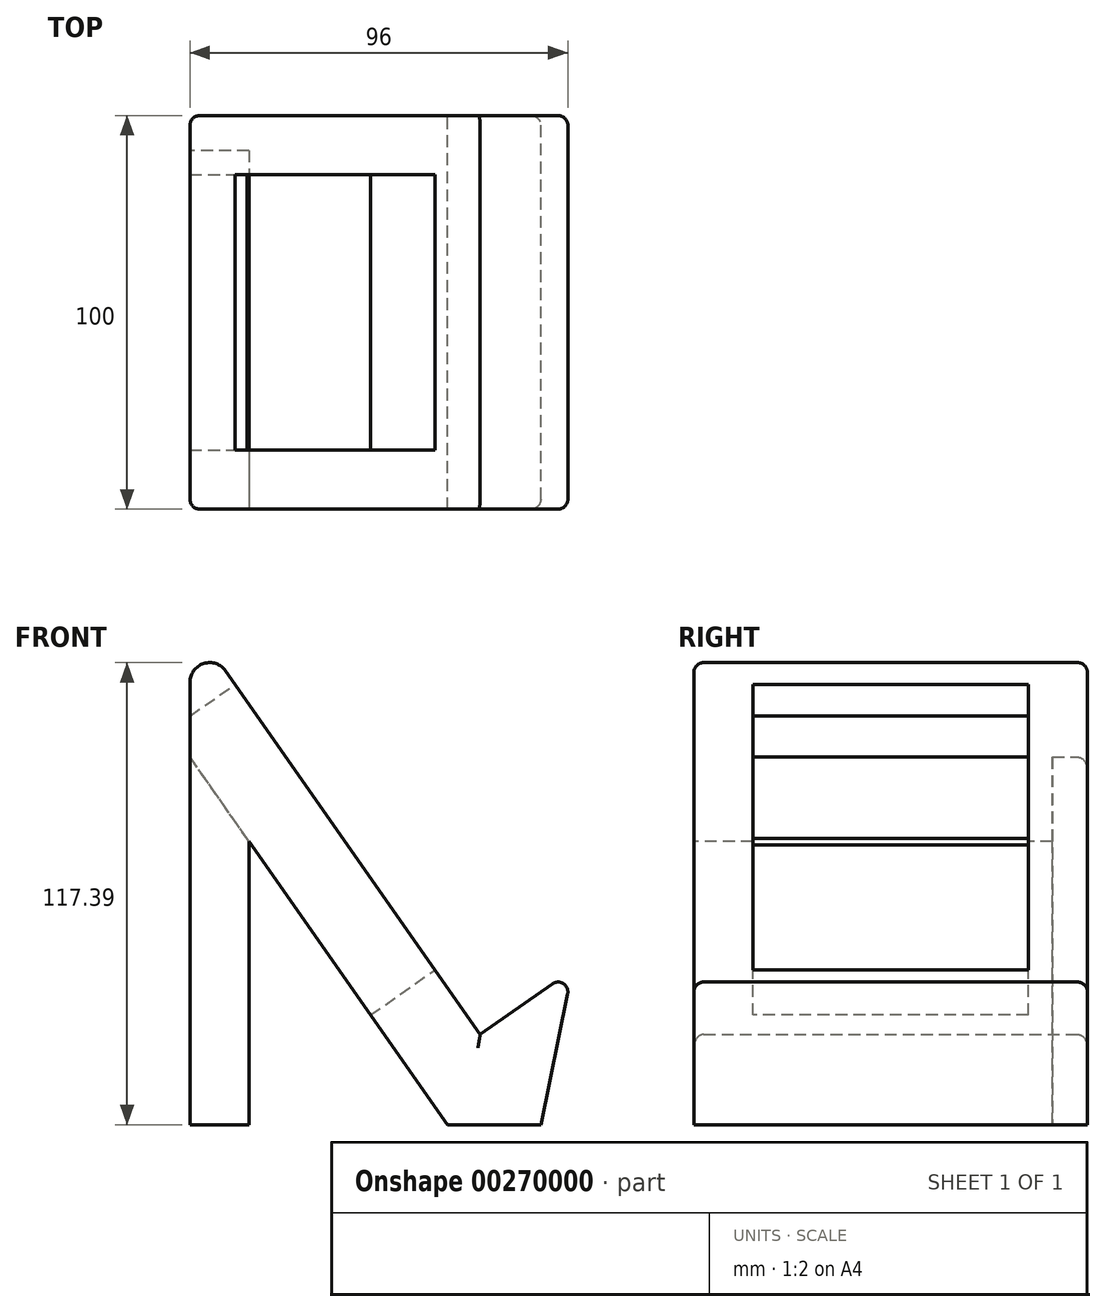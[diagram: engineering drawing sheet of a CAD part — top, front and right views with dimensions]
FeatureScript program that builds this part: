
annotation { "Feature Type Name" : "Feature", "Feature Type Description" : "" }
export const myFeature = defineFeature(function(context is Context, id is Id, definition is map)
    precondition{}
    {
        {
            var Q0;
            Q0=qCreatedBy(makeId("Front.planeOp"),FACE);
            var sketch = newSketch(context, id + "F0", { "sketchPlane" : qUnion([Q0])});
            skLineSegment(sketch, "E0", {"start": v(0, 0) * mm, "end": v(-73.74, 105.31) * mm});
            skLineSegment(sketch, "E1", {"start": v(15.38, -22.94) * mm, "end": v(-8.35, -22.94) * mm});
            skLineSegment(sketch, "E2", {"start": v(-8.35, -22.94) * mm, "end": v(-73.74, 70.44) * mm});
            skLineSegment(sketch, "E3", {"start": v(0, 0) * mm, "end": v(23.48, 16.44) * mm});
            skLineSegment(sketch, "E4", {"start": v(23.48, 16.44) * mm, "end": v(15.38, -22.94) * mm});
            skLineSegment(sketch, "E5", {"start": v(-73.74, 43.45) * mm, "end": v(-73.74, 105.31) * mm});
            skLineSegment(sketch, "E6", {"start": v(-73.74, -22.94) * mm, "end": v(-73.74, 43.45) * mm});
            skLineSegment(sketch, "E7", {"start": v(-73.74, -22.94) * mm, "end": v(-58.74, -22.94) * mm});
            skLineSegment(sketch, "E8", {"start": v(-58.74, -22.94) * mm, "end": v(-58.74, 83.9) * mm});
            skLineSegment(sketch, "E9", {"start": v(-58.74, -22.94) * mm, "end": v(-8.35, -22.94) * mm});
            skSolve(sketch);
        }
        {
            var Q0;
            {var subQ6=sQuery(id+"F0.wireOp",EDGE,"E1");Q0=makeQuery(id+"F0.imprint","IMPRINT",FACE,{"disambiguationData":[TD([[makeQuery(id+"F0.imprint","IMPRINT",EDGE,{"derivedFrom":subQ6}),-1.0]])]});}
            var Q1;
            {var subQ0=sQuery(id+"F0.wireOp",EDGE,"E5");var subQ1=sQuery(id+"F0.wireOp",EDGE,"E0");var subQ2=makeQuery(id+"F0.imprint","INTERSECT",VERTEX,{"derivedFrom":[subQ1,subQ0]});Q1=makeQuery(id+"F0.imprint","IMPRINT",FACE,{"disambiguationData":[TD([[makeQuery(id+"F0.imprint","IMPRINT",EDGE,{"disambiguationData":[TD([[subQ2,1.0]])],"derivedFrom":subQ1}),1.0]])]});}
            extrude(context, id + "F1", {"entities" : qUnion([Q0, Q1]), "endBound" : BoundingType.SYMMETRIC, "depth" : 100 * mm});
        }
        {
            var Q0;
            Q0=makeQuery(id+"F1.opExtrude","SWEPT_FACE",FACE,{"disambiguationData":[OSD([sQuery(id+"F0.wireOp",EDGE,"E0")])]});
            var sketch = newSketch(context, id + "F2", { "sketchPlane" : qUnion([Q0])});
            skLineSegment(sketch, "E10.0.0", {"start": v(50, 0) * mm, "end": v(50, 128.56) * mm});
            skLineSegment(sketch, "E10.0.1", {"start": v(50, 128.56) * mm, "end": v(-50, 128.56) * mm});
            skLineSegment(sketch, "E10.0.2", {"start": v(-50, 128.56) * mm, "end": v(-50, 0) * mm});
            skLineSegment(sketch, "E10.0.3", {"start": v(-50, 0) * mm, "end": v(50, 0) * mm});
            skLineSegment(sketch, "E11.0", {"start": v(35, 108.56) * mm, "end": v(-35, 108.56) * mm});
            skLineSegment(sketch, "E11.2", {"start": v(-35, 20) * mm, "end": v(35, 20) * mm});
            skLineSegment(sketch, "E12", {"start": v(-35, 108.56) * mm, "end": v(-35, 20) * mm});
            skLineSegment(sketch, "E13", {"start": v(35, 108.56) * mm, "end": v(35, 20) * mm});
            skSolve(sketch);
        }
        {
            var Q0;
            Q0=makeQuery(id+"F2.imprint","IMPRINT",FACE,{"disambiguationData":[TD([[makeQuery(id+"F2.imprint","IMPRINT",EDGE,{"derivedFrom":sQuery(id+"F2.wireOp",EDGE,"E11.0")}),1.0]])]});
            extrude(context, id + "F3", {"entities" : qUnion([Q0]), "operationType" : NewBodyOperationType.REMOVE, "endBound" : BoundingType.THROUGH_ALL, "oppositeDirection" : true, "depth" : 25 * mm});
        }
        {
            var Q0;
            Q0=makeQuery(id+"F1.opExtrude","CAP_FACE",FACE,{"disambiguationData":[OSD([sQuery(id+"F0.wireOp",EDGE,"E0"),sQuery(id+"F0.wireOp",EDGE,"E1"),sQuery(id+"F0.wireOp",EDGE,"E2"),sQuery(id+"F0.wireOp",EDGE,"E3"),sQuery(id+"F0.wireOp",EDGE,"E4"),sQuery(id+"F0.wireOp",EDGE,"E5")])],"isStart":false});
            var sketch = newSketch(context, id + "F4", { "sketchPlane" : qUnion([Q0])});
            skLineSegment(sketch, "E14.0.0", {"start": v(-58.74, -22.94) * mm, "end": v(-58.74, 49.02) * mm});
            skLineSegment(sketch, "E14.0.1", {"start": v(-58.74, 49.02) * mm, "end": v(-73.74, 70.44) * mm});
            skLineSegment(sketch, "E14.0.2", {"start": v(-73.74, 70.44) * mm, "end": v(-73.74, 43.45) * mm});
            skLineSegment(sketch, "E14.0.3", {"start": v(-73.74, 43.45) * mm, "end": v(-73.74, -22.94) * mm});
            skLineSegment(sketch, "E14.0.4", {"start": v(-73.74, -22.94) * mm, "end": v(-58.74, -22.94) * mm});
            skLineSegment(sketch, "E15.0.0", {"start": v(-73.74, 70.44) * mm, "end": v(-58.74, 49.02) * mm});
            skLineSegment(sketch, "E15.0.1", {"start": v(-58.74, 49.02) * mm, "end": v(-58.74, 83.9) * mm});
            skLineSegment(sketch, "E15.0.2", {"start": v(-58.74, 83.9) * mm, "end": v(-73.74, 105.31) * mm});
            skLineSegment(sketch, "E15.0.3", {"start": v(-73.74, 105.31) * mm, "end": v(-73.74, 70.44) * mm});
            skLineSegment(sketch, "E16.0.0", {"start": v(-58.74, 49.02) * mm, "end": v(-58.74, -22.94) * mm});
            skLineSegment(sketch, "E16.0.1", {"start": v(-58.74, -22.94) * mm, "end": v(-8.35, -22.94) * mm});
            skLineSegment(sketch, "E16.0.2", {"start": v(-8.35, -22.94) * mm, "end": v(-58.74, 49.02) * mm});
            skSolve(sketch);
        }
        {
            var Q0;
            Q0=makeQuery(id+"F4.imprint","IMPRINT",FACE,{"disambiguationData":[TD([[makeQuery(id+"F4.imprint","IMPRINT",EDGE,{"derivedFrom":sQuery(id+"F4.wireOp",EDGE,"E14.0.2")}),1.0]])]});
            var Q1;
            Q1=makeQuery(id+"F4.imprint","IMPRINT",FACE,{"disambiguationData":[TD([[makeQuery(id+"F4.imprint","IMPRINT",EDGE,{"derivedFrom":sQuery(id+"F4.wireOp",EDGE,"E16.0.0")}),1.0]])]});
            var Q2;
            Q2=makeQuery(id+"F4.imprint","IMPRINT",FACE,{"disambiguationData":[TD([[makeQuery(id+"F4.imprint","IMPRINT",EDGE,{"derivedFrom":sQuery(id+"F4.wireOp",EDGE,"E15.0.0")}),-1.0]])]});
            extrude(context, id + "F5", {"entities" : qUnion([Q0, Q1, Q2]), "operationType" : NewBodyOperationType.ADD, "oppositeDirection" : true, "depth" : 15 * mm});
        }
        {
            var Q0;
            Q0=makeQuery(id+"F1.opExtrude","CAP_FACE",FACE,{"disambiguationData":[OSD([sQuery(id+"F0.wireOp",EDGE,"E0"),sQuery(id+"F0.wireOp",EDGE,"E1"),sQuery(id+"F0.wireOp",EDGE,"E2"),sQuery(id+"F0.wireOp",EDGE,"E3"),sQuery(id+"F0.wireOp",EDGE,"E4"),sQuery(id+"F0.wireOp",EDGE,"E5")])],"isStart":true});
            var sketch = newSketch(context, id + "F6", { "sketchPlane" : qUnion([Q0])});
            skLineSegment(sketch, "E17.0.0", {"start": v(73.74, 70.44) * mm, "end": v(58.74, 49.02) * mm});
            skLineSegment(sketch, "E17.0.1", {"start": v(58.74, 49.02) * mm, "end": v(58.74, 83.9) * mm});
            skLineSegment(sketch, "E17.0.2", {"start": v(58.74, 83.9) * mm, "end": v(73.74, 105.31) * mm});
            skLineSegment(sketch, "E17.0.3", {"start": v(73.74, 105.31) * mm, "end": v(73.74, 70.44) * mm});
            skLineSegment(sketch, "E18.0.0", {"start": v(58.74, -22.94) * mm, "end": v(58.74, 49.02) * mm});
            skLineSegment(sketch, "E18.0.1", {"start": v(58.74, 49.02) * mm, "end": v(73.74, 70.44) * mm});
            skLineSegment(sketch, "E18.0.2", {"start": v(73.74, 70.44) * mm, "end": v(73.74, 43.45) * mm});
            skLineSegment(sketch, "E18.0.3", {"start": v(73.74, 43.45) * mm, "end": v(73.74, -22.94) * mm});
            skLineSegment(sketch, "E18.0.4", {"start": v(73.74, -22.94) * mm, "end": v(58.74, -22.94) * mm});
            skLineSegment(sketch, "E19.0.0", {"start": v(58.74, 49.02) * mm, "end": v(58.74, -22.94) * mm});
            skLineSegment(sketch, "E19.0.1", {"start": v(58.74, -22.94) * mm, "end": v(8.35, -22.94) * mm});
            skLineSegment(sketch, "E19.0.2", {"start": v(8.35, -22.94) * mm, "end": v(58.74, 49.02) * mm});
            skSolve(sketch);
        }
        {
            var Q0;
            Q0=makeQuery(id+"F6.imprint","IMPRINT",FACE,{"disambiguationData":[TD([[makeQuery(id+"F6.imprint","IMPRINT",EDGE,{"derivedFrom":sQuery(id+"F6.wireOp",EDGE,"E19.0.0")}),-1.0]])]});
            var Q1;
            Q1=makeQuery(id+"F6.imprint","IMPRINT",FACE,{"disambiguationData":[TD([[makeQuery(id+"F6.imprint","IMPRINT",EDGE,{"derivedFrom":sQuery(id+"F6.wireOp",EDGE,"E18.0.1")}),-1.0]])]});
            var Q2;
            Q2=makeQuery(id+"F6.imprint","IMPRINT",FACE,{"disambiguationData":[TD([[makeQuery(id+"F6.imprint","IMPRINT",EDGE,{"derivedFrom":sQuery(id+"F6.wireOp",EDGE,"E17.0.1")}),-1.0]])]});
            extrude(context, id + "F7", {"entities" : qUnion([Q0, Q1, Q2]), "operationType" : NewBodyOperationType.ADD, "oppositeDirection" : true, "depth" : 15 * mm});
        }
        {
            var Q0;
            Q0=makeQuery(id+"F4.imprint","IMPRINT",FACE,{"disambiguationData":[TD([[makeQuery(id+"F4.imprint","IMPRINT",EDGE,{"derivedFrom":sQuery(id+"F4.wireOp",EDGE,"E14.0.2")}),1.0]])]});
            var Q1;
            Q1=makeQuery(id+"F4.imprint","IMPRINT",FACE,{"disambiguationData":[TD([[makeQuery(id+"F4.imprint","IMPRINT",EDGE,{"derivedFrom":sQuery(id+"F4.wireOp",EDGE,"E15.0.0")}),-1.0]])]});
            extrude(context, id + "F8", {"entities" : qUnion([Q0, Q1]), "operationType" : NewBodyOperationType.ADD, "oppositeDirection" : true, "depth" : 91.1 * mm});
        }
        {
            var Q0;
            Q0=makeQuery(id+"F1.opExtrude","SWEPT_EDGE",EDGE,{"disambiguationData":[OSD([sQuery(id+"F0.wireOp",EDGE,"E0"),sQuery(id+"F0.wireOp",EDGE,"E5")])]});
            fillet(context, id + "F9", {"entities" : qUnion([Q0]), "radius" : 5 * mm, "tangentPropagation" : true, "allowEdgeOverflow" : false});
        }
        {
            var Q0;
            Q0=makeQuery(id+"F1.opExtrude","SWEPT_EDGE",EDGE,{"disambiguationData":[OSD([sQuery(id+"F0.wireOp",EDGE,"E3"),sQuery(id+"F0.wireOp",EDGE,"E4")])]});
            fillet(context, id + "F10", {"entities" : qUnion([Q0]), "radius" : 2.5 * mm, "tangentPropagation" : true, "allowEdgeOverflow" : false});
        }
        {
            var Q0;
            Q0=makeQuery(id+"F3.boolean.opBoolean","COPY",EDGE,{"derivedFrom":makeQuery(id+"F3.opExtrude","CAP_EDGE",EDGE,{"disambiguationData":[OSD([sQuery(id+"F2.wireOp",EDGE,"E12")])],"isStart":true})});
            var Q1;
            Q1=makeQuery(id+"F8.opExtrude","SWEPT_EDGE",EDGE,{"disambiguationData":[OSD([sQuery(id+"F0.wireOp",EDGE,"E0"),sQuery(id+"F4.wireOp",EDGE,"E15.0.1"),sQuery(id+"F4.wireOp",EDGE,"E15.0.2")])]});
            var Q2;
            Q2=makeQuery(id+"F3.boolean.opBoolean","COPY",EDGE,{"derivedFrom":makeQuery(id+"F3.opExtrude","CAP_EDGE",EDGE,{"disambiguationData":[OSD([sQuery(id+"F2.wireOp",EDGE,"E11.2")])],"isStart":true})});
            var Q3;
            Q3=makeQuery(id+"F3.boolean.opBoolean","COPY",EDGE,{"derivedFrom":makeQuery(id+"F3.opExtrude","CAP_EDGE",EDGE,{"disambiguationData":[OSD([sQuery(id+"F2.wireOp",EDGE,"E13")])],"isStart":true})});
            chamfer(context, id + "F11", {"entities" : qUnion([Q0, Q1, Q2, Q3]), "width" : 3 * mm, "tangentPropagation" : true});
        }
        {
            var Q0;
            Q0=makeQuery(id+"F1.opExtrude","CAP_EDGE",EDGE,{"disambiguationData":[OSD([sQuery(id+"F0.wireOp",EDGE,"E0")])],"isStart":false});
            var Q1;
            Q1=makeQuery(id+"F1.opExtrude","CAP_EDGE",EDGE,{"disambiguationData":[OSD([sQuery(id+"F0.wireOp",EDGE,"E3")])],"isStart":false});
            var Q2;
            Q2=makeQuery(id+"F1.opExtrude","CAP_EDGE",EDGE,{"disambiguationData":[OSD([sQuery(id+"F0.wireOp",EDGE,"E0")])],"isStart":true});
            var Q3;
            Q3=makeQuery(id+"F1.opExtrude","CAP_EDGE",EDGE,{"disambiguationData":[OSD([sQuery(id+"F0.wireOp",EDGE,"E3")])],"isStart":true});
            fillet(context, id + "F12", {"entities" : qUnion([Q0, Q1, Q2, Q3]), "radius" : 2.5 * mm, "tangentPropagation" : true, "allowEdgeOverflow" : false});
        }
    });
